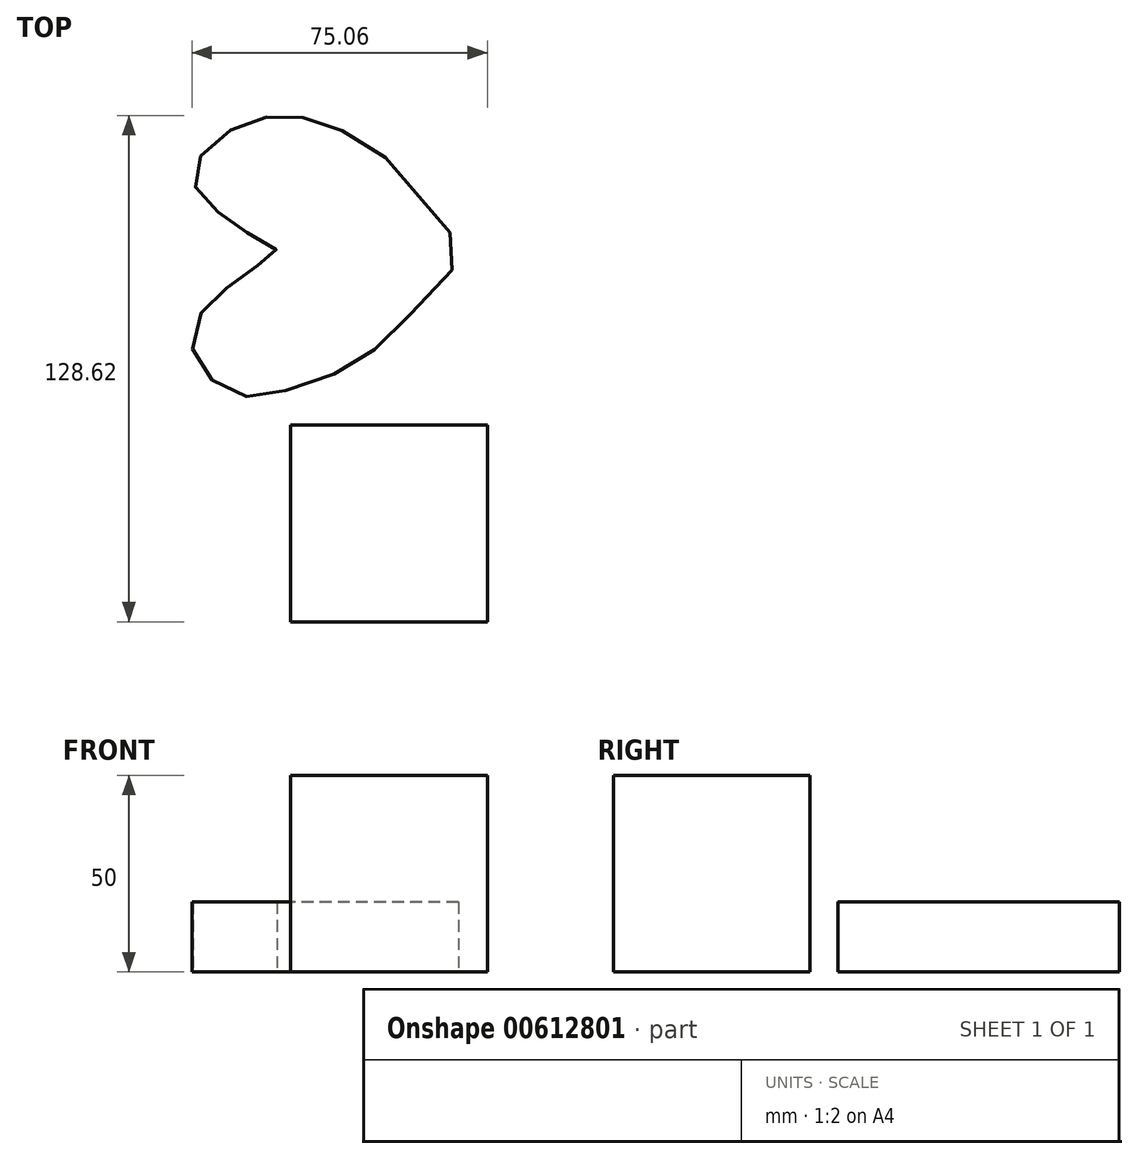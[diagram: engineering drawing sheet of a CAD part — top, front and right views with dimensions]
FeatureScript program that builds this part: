
annotation { "Feature Type Name" : "Feature", "Feature Type Description" : "" }
export const myFeature = defineFeature(function(context is Context, id is Id, definition is map)
    precondition{}
    {
        {
            var Q0;
            Q0=qCreatedBy(makeId("Top.planeOp"),FACE);
            var sketch = newSketch(context, id + "F0", { "sketchPlane" : qUnion([Q0])});
            skLineSegment(sketch, "E0.bottom", {"start": v(0, 0) * mm, "end": v(50, 0) * mm});
            skLineSegment(sketch, "E0.top", {"start": v(0, -50) * mm, "end": v(50, -50) * mm});
            skLineSegment(sketch, "E0.left", {"start": v(0, 0) * mm, "end": v(0, -50) * mm});
            skLineSegment(sketch, "E0.right", {"start": v(50, 0) * mm, "end": v(50, -50) * mm});
            skSolve(sketch);
        }
        {
            var Q0;
            Q0=makeQuery(id+"F0.imprint","IMPRINT",FACE,{"disambiguationData":[TD([[makeQuery(id+"F0.imprint","IMPRINT",EDGE,{"derivedFrom":sQuery(id+"F0.wireOp",EDGE,"E0.bottom")}),-1.0]])]});
            extrude(context, id + "F1", {"entities" : qUnion([Q0]), "depth" : 50 * mm, "offsetDistance" : 25 * mm});
        }
        {
            var Q0;
            Q0=qCreatedBy(makeId("Top.planeOp"),FACE);
            var sketch = newSketch(context, id + "F2", { "sketchPlane" : qUnion([Q0])});
            skFitSpline(sketch, "E1", {"points": [v(-11.11, 7.25) * mm, v(-20.37, 11.88) * mm, v(-25, 19.91) * mm, v(-22.23, 29.17) * mm, v(-15.43, 35.34) * mm, v(-7.1, 41.2) * mm, v(-3.4, 43.99) * mm, v(-8.33, 47.38) * mm, v(-16.05, 52.32) * mm, v(-22.53, 57.88) * mm, v(-24.7, 64.36) * mm, v(-19.14, 72.08) * mm, v(-9.88, 77.33) * mm, v(0, 78.56) * mm, v(9.88, 76.1) * mm, v(25, 67.14) * mm, v(36.43, 53.25) * mm, v(42.6, 43.37) * mm, v(28.7, 26.4) * mm, v(16.98, 15.9) * mm, v(0, 9.1) * mm, v(-11.11, 7.25) * mm]});
            skSolve(sketch);
        }
        {
            var Q0;
            Q0=makeQuery(id+"F2.imprint","IMPRINT",FACE,{"disambiguationData":[TD([[makeQuery(id+"F2.imprint","IMPRINT",EDGE,{"derivedFrom":sQuery(id+"F2.wireOp",EDGE,"E1")}),-1.0]])]});
            extrude(context, id + "F3", {"entities" : qUnion([Q0]), "depth" : 17.8 * mm, "offsetDistance" : 25 * mm});
        }
    });
